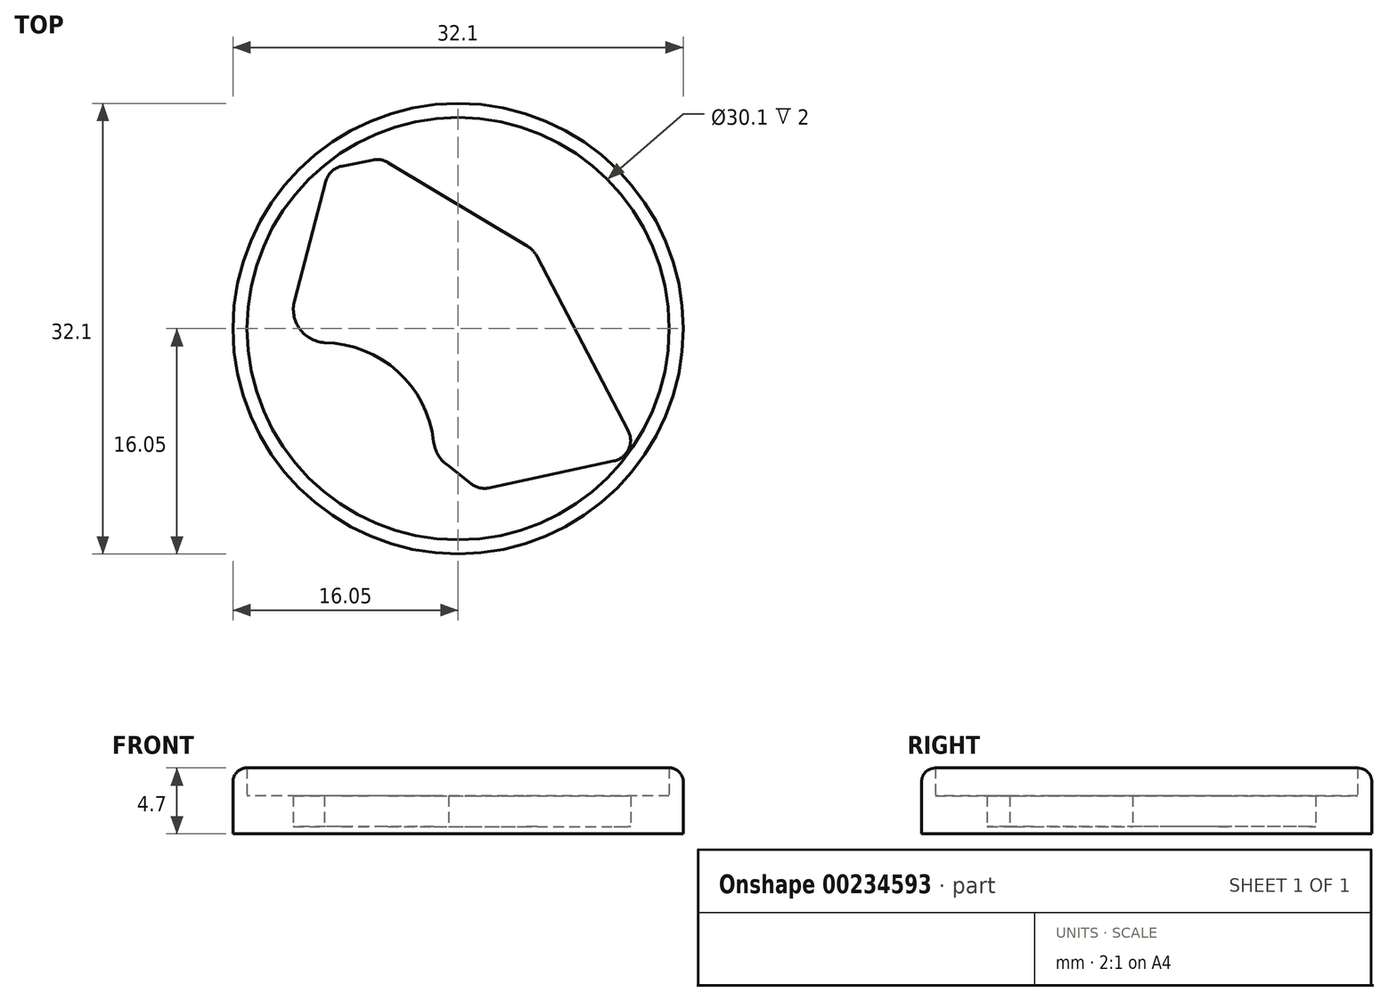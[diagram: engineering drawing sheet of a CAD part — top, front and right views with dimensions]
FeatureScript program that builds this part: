
annotation { "Feature Type Name" : "Feature", "Feature Type Description" : "" }
export const myFeature = defineFeature(function(context is Context, id is Id, definition is map)
    precondition{}
    {
        {
            var Q0;
            Q0=qCreatedBy(makeId("Top.planeOp"),FACE);
            var sketch = newSketch(context, id + "F0", { "sketchPlane" : qUnion([Q0])});
            skLineSegment(sketch, "E0", {"start": v(-8.87, 10.7) * mm, "end": v(11.18, -8.85) * mm, "construction": true});
            skLineSegment(sketch, "E1", {"start": v(-8.96, 10.36) * mm, "end": v(-11.19, 1.86) * mm});
            skLineSegment(sketch, "E2", {"start": v(-8.18, 11.09) * mm, "end": v(-5.96, 11.53) * mm});
            skLineSegment(sketch, "E3", {"start": v(-5.25, 11.4) * mm, "end": v(4.64, 5.48) * mm});
            skLineSegment(sketch, "E4", {"start": v(5.2, 4.9) * mm, "end": v(11.68, -7.5) * mm});
            skLineSegment(sketch, "E5", {"start": v(2.08, -10.86) * mm, "end": v(11, -8.94) * mm});
            skLineSegment(sketch, "E6", {"start": v(-0.67, -9.14) * mm, "end": v(1.25, -10.66) * mm});
            skArc(sketch, "E7", {"start": v(-11.19, 1.86) * mm, "mid": v(-10.9, 0.3) * mm, "end": v(-9.51, -0.5) * mm});
            skArc(sketch, "E8", {"start": v(-1.25, -8) * mm, "mid": v(-3.97, -2.7) * mm, "end": v(-9.51, -0.5) * mm});
            skArc(sketch, "E9", {"start": v(-1.25, -8) * mm, "mid": v(-1.06, -8.63) * mm, "end": v(-0.67, -9.14) * mm});
            skPoint(sketch, "E10.visualSharp", {"position": v(-5.58, 11.6) * mm});
            skArc(sketch, "E10.filletArc", {"start": v(-5.25, 11.4) * mm, "mid": v(-5.6, 11.54) * mm, "end": v(-5.96, 11.53) * mm});
            skPoint(sketch, "E11.visualSharp", {"position": v(5, 5.27) * mm});
            skArc(sketch, "E11.filletArc", {"start": v(5.2, 4.9) * mm, "mid": v(4.96, 5.23) * mm, "end": v(4.64, 5.48) * mm});
            skPoint(sketch, "E12.visualSharp", {"position": v(12.3, -8.66) * mm});
            skArc(sketch, "E12.filletArc", {"start": v(11, -8.94) * mm, "mid": v(11.7, -8.39) * mm, "end": v(11.68, -7.5) * mm});
            skPoint(sketch, "E13.visualSharp", {"position": v(1.62, -10.96) * mm});
            skArc(sketch, "E13.filletArc", {"start": v(1.25, -10.66) * mm, "mid": v(1.64, -10.85) * mm, "end": v(2.08, -10.86) * mm});
            skArc(sketch, "E14.filletArc", {"start": v(-8.18, 11.09) * mm, "mid": v(-8.67, 10.83) * mm, "end": v(-8.96, 10.36) * mm});
            skCircle(sketch, "E15", {"center": v(0, 0) * mm, "radius": 15.05 * mm, "construction": true});
            skCircle(sketch, "E16.0", {"center": v(0, 0) * mm, "radius": 16.05 * mm});
            skArc(sketch, "E17.0", {"start": v(-1.74, -8.06) * mm, "mid": v(-1.4, -9.04) * mm, "end": v(-0.68, -9.77) * mm});
            skArc(sketch, "E17.1", {"start": v(-1.74, -8.06) * mm, "mid": v(-4.3, -3.06) * mm, "end": v(-9.54, -1) * mm});
            skArc(sketch, "E17.2", {"start": v(-11.67, 1.99) * mm, "mid": v(-11.3, 0) * mm, "end": v(-9.54, -1) * mm});
            skLineSegment(sketch, "E17.3", {"start": v(5.64, 5.12) * mm, "end": v(12.13, -7.26) * mm});
            skArc(sketch, "E17.4", {"start": v(11.11, -9.43) * mm, "mid": v(12.16, -8.6) * mm, "end": v(12.13, -7.26) * mm});
            skLineSegment(sketch, "E17.5", {"start": v(2.18, -11.35) * mm, "end": v(11.11, -9.43) * mm});
            skArc(sketch, "E17.6", {"start": v(0.95, -11.06) * mm, "mid": v(1.53, -11.34) * mm, "end": v(2.18, -11.35) * mm});
            skArc(sketch, "E17.7", {"start": v(5.64, 5.12) * mm, "mid": v(5.32, 5.57) * mm, "end": v(4.9, 5.91) * mm});
            skLineSegment(sketch, "E17.8", {"start": v(-5, 11.84) * mm, "end": v(4.9, 5.91) * mm});
            skArc(sketch, "E17.9", {"start": v(-5, 11.84) * mm, "mid": v(-5.51, 12.03) * mm, "end": v(-6.06, 12.02) * mm});
            skLineSegment(sketch, "E17.10", {"start": v(-8.28, 11.58) * mm, "end": v(-6.06, 12.02) * mm});
            skArc(sketch, "E17.11", {"start": v(-8.28, 11.58) * mm, "mid": v(-9.02, 11.2) * mm, "end": v(-9.44, 10.49) * mm});
            skLineSegment(sketch, "E17.12", {"start": v(-9.44, 10.49) * mm, "end": v(-11.67, 1.99) * mm});
            skLineSegment(sketch, "E18", {"start": v(-0.68, -9.77) * mm, "end": v(0.95, -11.06) * mm});
            skSolve(sketch);
        }
        {
            var Q0;
            Q0=makeQuery(id+"F0.imprint","IMPRINT",FACE,{"disambiguationData":[TD([[makeQuery(id+"F0.imprint","IMPRINT",EDGE,{"derivedFrom":sQuery(id+"F0.wireOp",EDGE,"E16.0")}),1.0]])]});
            extrude(context, id + "F1", {"entities" : qUnion([Q0]), "depth" : 2.7 * mm});
        }
        {
            var Q0;
            Q0=makeQuery(id+"F1.opExtrude","CAP_FACE",FACE,{"disambiguationData":[OSD([sQuery(id+"F0.wireOp",EDGE,"E1"),sQuery(id+"F0.wireOp",EDGE,"E2"),sQuery(id+"F0.wireOp",EDGE,"E3"),sQuery(id+"F0.wireOp",EDGE,"E4"),sQuery(id+"F0.wireOp",EDGE,"E5"),sQuery(id+"F0.wireOp",EDGE,"E6"),sQuery(id+"F0.wireOp",EDGE,"E7"),sQuery(id+"F0.wireOp",EDGE,"E8"),sQuery(id+"F0.wireOp",EDGE,"E9"),sQuery(id+"F0.wireOp",EDGE,"E10.filletArc"),sQuery(id+"F0.wireOp",EDGE,"E11.filletArc"),sQuery(id+"F0.wireOp",EDGE,"E12.filletArc"),sQuery(id+"F0.wireOp",EDGE,"E13.filletArc"),sQuery(id+"F0.wireOp",EDGE,"E14.filletArc"),sQuery(id+"F0.wireOp",EDGE,"E16.0")])],"isStart":false});
            var sketch = newSketch(context, id + "F2", { "sketchPlane" : qUnion([Q0])});
            skCircle(sketch, "E19.0", {"center": v(0, 0) * mm, "radius": 16.05 * mm});
            skCircle(sketch, "E19.1", {"center": v(0, 0) * mm, "radius": 15.05 * mm});
            skSolve(sketch);
        }
        {
            var Q0;
            Q0 = qSketchRegion(id + "F2", true);
            extrude(context, id + "F3", {"entities" : qUnion([Q0]), "operationType" : NewBodyOperationType.ADD, "depth" : 2 * mm});
        }
        {
            var Q0;
            Q0=makeQuery(id+"F3.opExtrude","CAP_EDGE",EDGE,{"disambiguationData":[OSD([sQuery(id+"F2.wireOp",EDGE,"E19.0")])],"isStart":false});
            fillet(context, id + "F4", {"entities" : qUnion([Q0]), "radius" : 1 * mm, "tangentPropagation" : true, "allowEdgeOverflow" : false});
        }
        {
            var Q0;
            Q0=makeQuery(id+"F0.imprint","IMPRINT",FACE,{"disambiguationData":[TD([[makeQuery(id+"F0.imprint","IMPRINT",EDGE,{"derivedFrom":sQuery(id+"F0.wireOp",EDGE,"E1")}),-1.0]])]});
            var sketch = newSketch(context, id + "F5", { "sketchPlane" : qUnion([Q0])});
            skCircle(sketch, "E20.0", {"center": v(0, 0) * mm, "radius": 16.05 * mm});
            skSolve(sketch);
        }
        {
            var Q0;
            Q0 = qSketchRegion(id + "F5", true);
            extrude(context, id + "F6", {"entities" : qUnion([Q0]), "operationType" : NewBodyOperationType.ADD, "depth" : 0.5 * mm});
        }
    });
